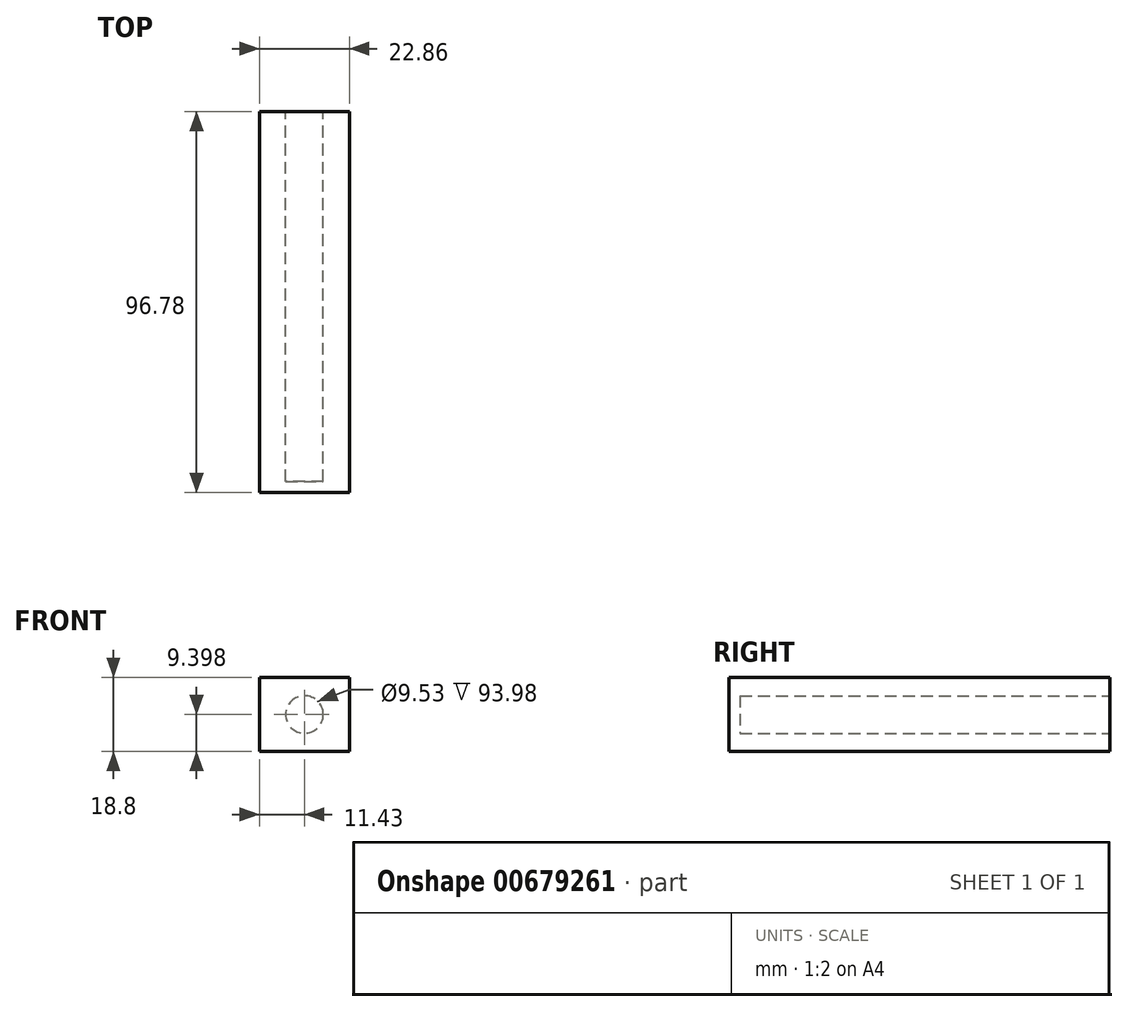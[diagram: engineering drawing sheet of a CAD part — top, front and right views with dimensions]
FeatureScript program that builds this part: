
annotation { "Feature Type Name" : "Feature", "Feature Type Description" : "" }
export const myFeature = defineFeature(function(context is Context, id is Id, definition is map)
    precondition{}
    {
        {
            var Q0;
            Q0=qCreatedBy(makeId("Top.planeOp"),FACE);
            var sketch = newSketch(context, id + "F0", { "sketchPlane" : qUnion([Q0])});
            skLineSegment(sketch, "E0.bottom", {"start": v(11.43, 48.39) * mm, "end": v(-11.43, 48.39) * mm});
            skLineSegment(sketch, "E0.top", {"start": v(11.43, -48.39) * mm, "end": v(-11.43, -48.39) * mm});
            skLineSegment(sketch, "E0.left", {"start": v(11.43, 48.39) * mm, "end": v(11.43, -48.39) * mm});
            skLineSegment(sketch, "E0.right", {"start": v(-11.43, 48.39) * mm, "end": v(-11.43, -48.39) * mm});
            skPoint(sketch, "E0.middle", {"position": v(0, 0) * mm});
            skSolve(sketch);
        }
        {
            var Q0;
            Q0=qSketchRegion(id+"F0",true);
            extrude(context, id + "F1", {"entities" : qUnion([Q0]), "depth" : 18.8 * mm, "offsetDistance" : 25.4 * mm});
        }
        {
            var Q0;
            Q0=makeQuery(id+"F1.opExtrude","SWEPT_FACE",FACE,{"disambiguationData":[OSD([sQuery(id+"F0.wireOp",EDGE,"E0.bottom")])]});
            var sketch = newSketch(context, id + "F2", { "sketchPlane" : qUnion([Q0])});
            skCircle(sketch, "E1", {"center": v(0, 9.4) * mm, "radius": 4.76 * mm});
            skPoint(sketch, "E1.centerSnap0", {"position": v(-11.43, 9.4) * mm});
            skSolve(sketch);
        }
        {
            var Q0;
            Q0=qSketchRegion(id+"F2",true);
            extrude(context, id + "F3", {"entities" : qUnion([Q0]), "operationType" : NewBodyOperationType.REMOVE, "oppositeDirection" : true, "depth" : 93.98 * mm, "offsetDistance" : 25.4 * mm});
        }
    });
